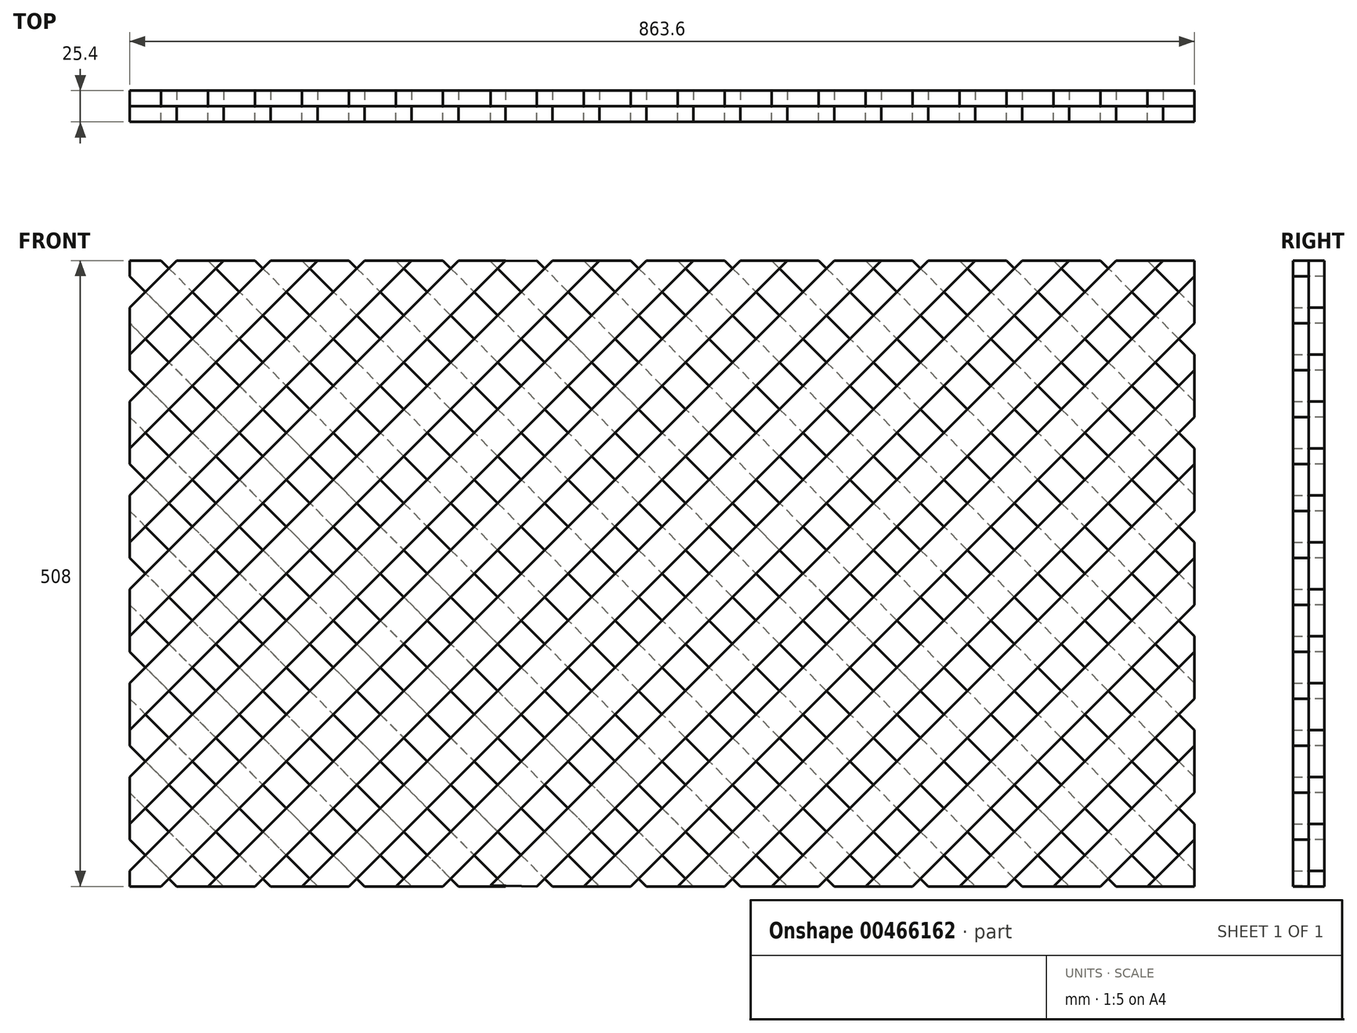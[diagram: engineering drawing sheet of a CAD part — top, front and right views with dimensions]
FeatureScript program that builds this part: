
annotation { "Feature Type Name" : "Feature", "Feature Type Description" : "" }
export const myFeature = defineFeature(function(context is Context, id is Id, definition is map)
    precondition{}
    {
        {
            var Q0;
            Q0=qCreatedBy(makeId("Front.planeOp"),FACE);
            var sketch = newSketch(context, id + "F0", { "sketchPlane" : qUnion([Q0])});
            skLineSegment(sketch, "E0.bottom", {"start": v(0, 0) * mm, "end": v(25.4, 0) * mm});
            skLineSegment(sketch, "E0.top", {"start": v(38.1, 508) * mm, "end": v(76.2, 508) * mm});
            skLineSegment(sketch, "E0.left", {"start": v(0, 0) * mm, "end": v(0, 12.7) * mm});
            skLineSegment(sketch, "E1", {"start": v(76.2, 508) * mm, "end": v(0, 431.8) * mm});
            skLineSegment(sketch, "E2", {"start": v(38.1, 393.7) * mm, "end": v(152.4, 508) * mm});
            skLineSegment(sketch, "E3", {"start": v(0, 355.6) * mm, "end": v(38.1, 393.7) * mm});
            skLineSegment(sketch, "E4", {"start": v(0, 279.4) * mm, "end": v(190.5, 469.9) * mm});
            skLineSegment(sketch, "E5", {"start": v(0, 203.2) * mm, "end": v(190.5, 393.7) * mm});
            skLineSegment(sketch, "E6", {"start": v(0, 127) * mm, "end": v(190.5, 317.5) * mm});
            skLineSegment(sketch, "E7", {"start": v(0, 50.8) * mm, "end": v(190.5, 241.3) * mm});
            skLineSegment(sketch, "E8", {"start": v(190.5, 165.1) * mm, "end": v(38.1, 12.7) * mm});
            skLineSegment(sketch, "E9", {"start": v(38.1, 12.7) * mm, "end": v(25.4, 0) * mm});
            skLineSegment(sketch, "E10", {"start": v(0, 469.9) * mm, "end": v(38.1, 508) * mm});
            skLineSegment(sketch, "E11", {"start": v(0, 393.7) * mm, "end": v(114.3, 508) * mm});
            skLineSegment(sketch, "E12", {"start": v(0, 317.5) * mm, "end": v(190.5, 508) * mm});
            skLineSegment(sketch, "E13", {"start": v(0, 241.3) * mm, "end": v(190.5, 431.8) * mm});
            skLineSegment(sketch, "E14", {"start": v(0, 165.1) * mm, "end": v(190.5, 355.6) * mm});
            skLineSegment(sketch, "E15", {"start": v(0, 88.9) * mm, "end": v(190.5, 279.4) * mm});
            skLineSegment(sketch, "E16", {"start": v(0, 12.7) * mm, "end": v(190.5, 203.2) * mm});
            skLineSegment(sketch, "E17", {"start": v(76.2, 12.7) * mm, "end": v(190.5, 127) * mm});
            skLineSegment(sketch, "E18", {"start": v(76.2, 12.7) * mm, "end": v(63.5, 0) * mm});
            skLineSegment(sketch, "E19", {"start": v(190.5, 88.9) * mm, "end": v(114.3, 12.7) * mm});
            skLineSegment(sketch, "E20", {"start": v(114.3, 12.7) * mm, "end": v(101.6, 0) * mm});
            skLineSegment(sketch, "E21", {"start": v(152.4, 12.7) * mm, "end": v(190.5, 50.8) * mm});
            skLineSegment(sketch, "E22", {"start": v(152.4, 12.7) * mm, "end": v(139.7, 0) * mm});
            skLineSegment(sketch, "E23", {"start": v(0, 431.8) * mm, "end": v(0, 469.9) * mm});
            skLineSegment(sketch, "E24", {"start": v(190.5, 12.7) * mm, "end": v(177.8, 0) * mm});
            skLineSegment(sketch, "E25.trimOffspring", {"start": v(139.7, 0) * mm, "end": v(177.8, 0) * mm});
            skLineSegment(sketch, "E26.trimOffspring", {"start": v(63.5, 0) * mm, "end": v(101.6, 0) * mm});
            skLineSegment(sketch, "E27.trimOffspring", {"start": v(0, 50.8) * mm, "end": v(0, 88.9) * mm});
            skLineSegment(sketch, "E28.trimOffspring", {"start": v(0, 127) * mm, "end": v(0, 165.1) * mm});
            skLineSegment(sketch, "E29.trimOffspring", {"start": v(0, 203.2) * mm, "end": v(0, 241.3) * mm});
            skLineSegment(sketch, "E30.trimOffspring", {"start": v(0, 355.6) * mm, "end": v(0, 393.7) * mm});
            skLineSegment(sketch, "E31.trimOffspring", {"start": v(114.3, 508) * mm, "end": v(152.4, 508) * mm});
            skLineSegment(sketch, "E32.1.0.1", {"start": v(190.5, 279.4) * mm, "end": v(381, 469.9) * mm});
            skLineSegment(sketch, "E32.1.0.3", {"start": v(190.5, 165.1) * mm, "end": v(381, 355.6) * mm});
            skLineSegment(sketch, "E32.1.0.4", {"start": v(190.5, 469.9) * mm, "end": v(228.6, 508) * mm});
            skLineSegment(sketch, "E32.1.0.5", {"start": v(190.5, 241.3) * mm, "end": v(381, 431.8) * mm});
            skLineSegment(sketch, "E32.1.0.7", {"start": v(190.5, 127) * mm, "end": v(381, 317.5) * mm});
            skLineSegment(sketch, "E32.1.0.8", {"start": v(381, 165.1) * mm, "end": v(228.6, 12.7) * mm});
            skLineSegment(sketch, "E32.1.0.11", {"start": v(190.5, 12.7) * mm, "end": v(381, 203.2) * mm});
            skLineSegment(sketch, "E32.1.0.14", {"start": v(266.7, 12.7) * mm, "end": v(381, 127) * mm});
            skLineSegment(sketch, "E32.1.0.15", {"start": v(190.5, 50.8) * mm, "end": v(381, 241.3) * mm});
            skLineSegment(sketch, "E32.1.0.18", {"start": v(190.5, 203.2) * mm, "end": v(381, 393.7) * mm});
            skLineSegment(sketch, "E32.1.0.19", {"start": v(342.9, 12.7) * mm, "end": v(381, 50.8) * mm});
            skLineSegment(sketch, "E32.1.0.24", {"start": v(190.5, 88.9) * mm, "end": v(381, 279.4) * mm});
            skLineSegment(sketch, "E32.1.0.25", {"start": v(381, 88.9) * mm, "end": v(304.8, 12.7) * mm});
            skLineSegment(sketch, "E32.1.0.28", {"start": v(190.5, 317.5) * mm, "end": v(381, 508) * mm});
            skLineSegment(sketch, "E32.1.0.30", {"start": v(190.5, 393.7) * mm, "end": v(304.8, 508) * mm});
            skLineSegment(sketch, "E32.1.0.32", {"start": v(190.5, 355.6) * mm, "end": v(228.6, 393.7) * mm});
            skLineSegment(sketch, "E32.1.0.33", {"start": v(228.6, 393.7) * mm, "end": v(342.9, 508) * mm});
            skLineSegment(sketch, "E32.1.0.34", {"start": v(266.7, 508) * mm, "end": v(190.5, 431.8) * mm});
            skLineSegment(sketch, "E32.1.0.36", {"start": v(266.7, 12.7) * mm, "end": v(254, 0) * mm});
            skLineSegment(sketch, "E32.1.0.37", {"start": v(228.6, 12.7) * mm, "end": v(215.9, 0) * mm});
            skLineSegment(sketch, "E32.1.0.39", {"start": v(342.9, 12.7) * mm, "end": v(330.2, 0) * mm});
            skLineSegment(sketch, "E32.1.0.40", {"start": v(381, 12.7) * mm, "end": v(368.3, 0) * mm});
            skLineSegment(sketch, "E32.1.0.41", {"start": v(304.8, 12.7) * mm, "end": v(292.1, 0) * mm});
            skLineSegment(sketch, "E32.2.0.1", {"start": v(381, 279.4) * mm, "end": v(571.5, 469.9) * mm});
            skLineSegment(sketch, "E32.2.0.3", {"start": v(381, 165.1) * mm, "end": v(571.5, 355.6) * mm});
            skLineSegment(sketch, "E32.2.0.4", {"start": v(381, 469.9) * mm, "end": v(419.1, 508) * mm});
            skLineSegment(sketch, "E32.2.0.5", {"start": v(381, 241.3) * mm, "end": v(571.5, 431.8) * mm});
            skLineSegment(sketch, "E32.2.0.7", {"start": v(381, 127) * mm, "end": v(571.5, 317.5) * mm});
            skLineSegment(sketch, "E32.2.0.8", {"start": v(571.5, 165.1) * mm, "end": v(419.1, 12.7) * mm});
            skLineSegment(sketch, "E32.2.0.11", {"start": v(381, 12.7) * mm, "end": v(571.5, 203.2) * mm});
            skLineSegment(sketch, "E32.2.0.12", {"start": v(495.3, 508) * mm, "end": v(533.4, 508) * mm});
            skLineSegment(sketch, "E32.2.0.14", {"start": v(457.2, 12.7) * mm, "end": v(571.5, 127) * mm});
            skLineSegment(sketch, "E32.2.0.15", {"start": v(381, 50.8) * mm, "end": v(571.5, 241.3) * mm});
            skLineSegment(sketch, "E32.2.0.18", {"start": v(381, 203.2) * mm, "end": v(571.5, 393.7) * mm});
            skLineSegment(sketch, "E32.2.0.19", {"start": v(533.4, 12.7) * mm, "end": v(571.5, 50.8) * mm});
            skLineSegment(sketch, "E32.2.0.21", {"start": v(444.5, 0) * mm, "end": v(482.6, 0) * mm});
            skLineSegment(sketch, "E32.2.0.24", {"start": v(381, 88.9) * mm, "end": v(571.5, 279.4) * mm});
            skLineSegment(sketch, "E32.2.0.25", {"start": v(571.5, 88.9) * mm, "end": v(495.3, 12.7) * mm});
            skLineSegment(sketch, "E32.2.0.28", {"start": v(381, 317.5) * mm, "end": v(571.5, 508) * mm});
            skLineSegment(sketch, "E32.2.0.29", {"start": v(520.7, 0) * mm, "end": v(558.8, 0) * mm});
            skLineSegment(sketch, "E32.2.0.30", {"start": v(381, 393.7) * mm, "end": v(495.3, 508) * mm});
            skLineSegment(sketch, "E32.2.0.31", {"start": v(419.1, 508) * mm, "end": v(457.2, 508) * mm});
            skLineSegment(sketch, "E32.2.0.32", {"start": v(381, 355.6) * mm, "end": v(419.1, 393.7) * mm});
            skLineSegment(sketch, "E32.2.0.33", {"start": v(419.1, 393.7) * mm, "end": v(533.4, 508) * mm});
            skLineSegment(sketch, "E32.2.0.34", {"start": v(457.2, 508) * mm, "end": v(381, 431.8) * mm});
            skLineSegment(sketch, "E32.2.0.35", {"start": v(381, 0) * mm, "end": v(406.4, 0) * mm});
            skLineSegment(sketch, "E32.2.0.36", {"start": v(457.2, 12.7) * mm, "end": v(444.5, 0) * mm});
            skLineSegment(sketch, "E32.2.0.37", {"start": v(419.1, 12.7) * mm, "end": v(406.4, 0) * mm});
            skLineSegment(sketch, "E32.2.0.39", {"start": v(533.4, 12.7) * mm, "end": v(520.7, 0) * mm});
            skLineSegment(sketch, "E32.2.0.40", {"start": v(571.5, 12.7) * mm, "end": v(558.8, 0) * mm});
            skLineSegment(sketch, "E32.2.0.41", {"start": v(495.3, 12.7) * mm, "end": v(482.6, 0) * mm});
            skLineSegment(sketch, "E32.3.0.1", {"start": v(571.5, 279.4) * mm, "end": v(762, 469.9) * mm});
            skLineSegment(sketch, "E32.3.0.3", {"start": v(571.5, 165.1) * mm, "end": v(762, 355.6) * mm});
            skLineSegment(sketch, "E32.3.0.4", {"start": v(571.5, 469.9) * mm, "end": v(609.6, 508) * mm});
            skLineSegment(sketch, "E32.3.0.5", {"start": v(571.5, 241.3) * mm, "end": v(762, 431.8) * mm});
            skLineSegment(sketch, "E32.3.0.7", {"start": v(571.5, 127) * mm, "end": v(762, 317.5) * mm});
            skLineSegment(sketch, "E32.3.0.8", {"start": v(762, 165.1) * mm, "end": v(609.6, 12.7) * mm});
            skLineSegment(sketch, "E32.3.0.11", {"start": v(571.5, 12.7) * mm, "end": v(762, 203.2) * mm});
            skLineSegment(sketch, "E32.3.0.14", {"start": v(647.7, 12.7) * mm, "end": v(762, 127) * mm});
            skLineSegment(sketch, "E32.3.0.15", {"start": v(571.5, 50.8) * mm, "end": v(762, 241.3) * mm});
            skLineSegment(sketch, "E32.3.0.18", {"start": v(571.5, 203.2) * mm, "end": v(762, 393.7) * mm});
            skLineSegment(sketch, "E32.3.0.19", {"start": v(723.9, 12.7) * mm, "end": v(762, 50.8) * mm});
            skLineSegment(sketch, "E32.3.0.24", {"start": v(571.5, 88.9) * mm, "end": v(762, 279.4) * mm});
            skLineSegment(sketch, "E32.3.0.25", {"start": v(762, 88.9) * mm, "end": v(685.8, 12.7) * mm});
            skLineSegment(sketch, "E32.3.0.28", {"start": v(571.5, 317.5) * mm, "end": v(762, 508) * mm});
            skLineSegment(sketch, "E32.3.0.30", {"start": v(571.5, 393.7) * mm, "end": v(685.8, 508) * mm});
            skLineSegment(sketch, "E32.3.0.32", {"start": v(571.5, 355.6) * mm, "end": v(609.6, 393.7) * mm});
            skLineSegment(sketch, "E32.3.0.33", {"start": v(609.6, 393.7) * mm, "end": v(723.9, 508) * mm});
            skLineSegment(sketch, "E32.3.0.34", {"start": v(647.7, 508) * mm, "end": v(571.5, 431.8) * mm});
            skLineSegment(sketch, "E32.3.0.36", {"start": v(647.7, 12.7) * mm, "end": v(635, 0) * mm});
            skLineSegment(sketch, "E32.3.0.37", {"start": v(609.6, 12.7) * mm, "end": v(596.9, 0) * mm});
            skLineSegment(sketch, "E32.3.0.39", {"start": v(723.9, 12.7) * mm, "end": v(711.2, 0) * mm});
            skLineSegment(sketch, "E32.3.0.40", {"start": v(762, 12.7) * mm, "end": v(749.3, 0) * mm});
            skLineSegment(sketch, "E32.3.0.41", {"start": v(685.8, 12.7) * mm, "end": v(673.1, 0) * mm});
            skLineSegment(sketch, "E32.4.0.1", {"start": v(762, 279.4) * mm, "end": v(863.6, 381) * mm});
            skLineSegment(sketch, "E32.4.0.3", {"start": v(762, 165.1) * mm, "end": v(863.6, 266.7) * mm});
            skLineSegment(sketch, "E32.4.0.4", {"start": v(762, 469.9) * mm, "end": v(800.1, 508) * mm});
            skLineSegment(sketch, "E32.4.0.5", {"start": v(762, 241.3) * mm, "end": v(863.6, 342.9) * mm});
            skLineSegment(sketch, "E32.4.0.7", {"start": v(762, 127) * mm, "end": v(863.6, 228.6) * mm});
            skLineSegment(sketch, "E32.4.0.8", {"start": v(863.6, 76.2) * mm, "end": v(800.1, 12.7) * mm});
            skLineSegment(sketch, "E32.4.0.11", {"start": v(762, 12.7) * mm, "end": v(863.6, 114.3) * mm});
            skLineSegment(sketch, "E32.4.0.14", {"start": v(838.2, 12.7) * mm, "end": v(863.6, 38.1) * mm});
            skLineSegment(sketch, "E32.4.0.15", {"start": v(762, 50.8) * mm, "end": v(863.6, 152.4) * mm});
            skLineSegment(sketch, "E32.4.0.18", {"start": v(762, 203.2) * mm, "end": v(863.6, 304.8) * mm});
            skLineSegment(sketch, "E32.4.0.21", {"start": v(825.5, 0) * mm, "end": v(863.6, 0) * mm});
            skLineSegment(sketch, "E32.4.0.24", {"start": v(762, 88.9) * mm, "end": v(863.6, 190.5) * mm});
            skLineSegment(sketch, "E32.4.0.28", {"start": v(762, 317.5) * mm, "end": v(863.6, 419.1) * mm});
            skLineSegment(sketch, "E32.4.0.30", {"start": v(762, 393.7) * mm, "end": v(863.6, 495.3) * mm});
            skLineSegment(sketch, "E32.4.0.31", {"start": v(800.1, 508) * mm, "end": v(838.2, 508) * mm});
            skLineSegment(sketch, "E32.4.0.32", {"start": v(762, 355.6) * mm, "end": v(800.1, 393.7) * mm});
            skLineSegment(sketch, "E32.4.0.33", {"start": v(800.1, 393.7) * mm, "end": v(863.6, 457.2) * mm});
            skLineSegment(sketch, "E32.4.0.34", {"start": v(838.2, 508) * mm, "end": v(762, 431.8) * mm});
            skLineSegment(sketch, "E32.4.0.35", {"start": v(762, 0) * mm, "end": v(787.4, 0) * mm});
            skLineSegment(sketch, "E32.4.0.36", {"start": v(838.2, 12.7) * mm, "end": v(825.5, 0) * mm});
            skLineSegment(sketch, "E32.4.0.37", {"start": v(800.1, 12.7) * mm, "end": v(787.4, 0) * mm});
            skLineSegment(sketch, "E32.direction1", {"start": v(0, 0) * mm, "end": v(177.8, 0) * mm, "construction": true});
            skLineSegment(sketch, "E33", {"start": v(190.5, 508) * mm, "end": v(228.6, 508) * mm});
            skLineSegment(sketch, "E34", {"start": v(266.7, 508) * mm, "end": v(304.8, 508) * mm});
            skLineSegment(sketch, "E35", {"start": v(342.9, 508) * mm, "end": v(381, 508) * mm});
            skLineSegment(sketch, "E36", {"start": v(215.9, 0) * mm, "end": v(254, 0) * mm});
            skLineSegment(sketch, "E37", {"start": v(292.21, 0.73) * mm, "end": v(330.2, 0) * mm});
            skLineSegment(sketch, "E38", {"start": v(368.3, 0) * mm, "end": v(381, 0) * mm});
            skLineSegment(sketch, "E39", {"start": v(0, 317.5) * mm, "end": v(0, 279.4) * mm});
            skLineSegment(sketch, "E40", {"start": v(762, 508) * mm, "end": v(723.9, 508) * mm});
            skLineSegment(sketch, "E41", {"start": v(685.8, 508) * mm, "end": v(647.7, 508) * mm});
            skLineSegment(sketch, "E42", {"start": v(609.6, 508) * mm, "end": v(571.5, 508) * mm});
            skLineSegment(sketch, "E43", {"start": v(762, 0) * mm, "end": v(749.3, 0) * mm});
            skLineSegment(sketch, "E44", {"start": v(596.9, 0) * mm, "end": v(635, 0) * mm});
            skLineSegment(sketch, "E45", {"start": v(673.1, 0) * mm, "end": v(711.2, 0) * mm});
            skLineSegment(sketch, "E46.0", {"start": v(863.6, 0) * mm, "end": v(863.6, 38.1) * mm});
            skLineSegment(sketch, "E47", {"start": v(863.6, 495.3) * mm, "end": v(863.6, 453.94) * mm});
            skLineSegment(sketch, "E48.trimOffspring", {"start": v(863.6, 381) * mm, "end": v(863.6, 419.1) * mm});
            skLineSegment(sketch, "E49.trimOffspring", {"start": v(863.6, 304.8) * mm, "end": v(863.6, 342.9) * mm});
            skLineSegment(sketch, "E50.trimOffspring", {"start": v(863.6, 228.6) * mm, "end": v(863.6, 266.7) * mm});
            skLineSegment(sketch, "E51.trimOffspring", {"start": v(863.6, 152.4) * mm, "end": v(863.6, 190.5) * mm});
            skLineSegment(sketch, "E52.trimOffspring", {"start": v(863.6, 76.2) * mm, "end": v(863.6, 114.3) * mm});
            skSolve(sketch);
        }
        {
            var Q0;
            Q0 = qSketchRegion(id + "F0", true);
            extrude(context, id + "F1", {"entities" : qUnion([Q0]), "depth" : 12.7 * mm});
        }
        {
            var Q0;
            Q0=qCreatedBy(makeId("Front.planeOp"),FACE);
            var sketch = newSketch(context, id + "F2", { "sketchPlane" : qUnion([Q0])});
            skLineSegment(sketch, "E53.MirrorCS", {"start": v(139.7, 508) * mm, "end": v(177.8, 508) * mm});
            skLineSegment(sketch, "E54.MirrorCS", {"start": v(63.5, 508) * mm, "end": v(101.6, 508) * mm});
            skLineSegment(sketch, "E55.MirrorCS", {"start": v(0, 508) * mm, "end": v(25.4, 508) * mm});
            skLineSegment(sketch, "E56.MirrorCS", {"start": v(0, 508) * mm, "end": v(0, 495.3) * mm});
            skLineSegment(sketch, "E57.MirrorCS", {"start": v(190.5, 495.3) * mm, "end": v(177.8, 508) * mm});
            skLineSegment(sketch, "E58.MirrorCS", {"start": v(685.8, 495.3) * mm, "end": v(673.1, 508) * mm});
            skLineSegment(sketch, "E59.MirrorCS", {"start": v(381, 508) * mm, "end": v(406.4, 508) * mm});
            skLineSegment(sketch, "E60.MirrorCS", {"start": v(457.2, 495.3) * mm, "end": v(444.5, 508) * mm});
            skLineSegment(sketch, "E61.MirrorCS", {"start": v(762, 508) * mm, "end": v(787.4, 508) * mm});
            skLineSegment(sketch, "E62.MirrorCS", {"start": v(762, 508) * mm, "end": v(749.3, 508) * mm});
            skLineSegment(sketch, "E63.MirrorCS", {"start": v(596.9, 508) * mm, "end": v(635, 508) * mm});
            skLineSegment(sketch, "E64.MirrorCS", {"start": v(838.2, 495.3) * mm, "end": v(825.5, 508) * mm});
            skLineSegment(sketch, "E65.MirrorCS", {"start": v(419.1, 495.3) * mm, "end": v(406.4, 508) * mm});
            skLineSegment(sketch, "E66.MirrorCS", {"start": v(533.4, 495.3) * mm, "end": v(520.7, 508) * mm});
            skLineSegment(sketch, "E67.MirrorCS", {"start": v(673.1, 508) * mm, "end": v(711.2, 508) * mm});
            skLineSegment(sketch, "E68.MirrorCS", {"start": v(800.1, 495.3) * mm, "end": v(787.4, 508) * mm});
            skLineSegment(sketch, "E69.MirrorCS", {"start": v(571.5, 495.3) * mm, "end": v(558.8, 508) * mm});
            skLineSegment(sketch, "E70.MirrorCS", {"start": v(76.2, 495.3) * mm, "end": v(63.5, 508) * mm});
            skLineSegment(sketch, "E71.MirrorCS", {"start": v(495.3, 495.3) * mm, "end": v(482.6, 508) * mm});
            skLineSegment(sketch, "E72.MirrorCS", {"start": v(266.7, 495.3) * mm, "end": v(254, 508) * mm});
            skLineSegment(sketch, "E73.MirrorCS", {"start": v(444.5, 508) * mm, "end": v(482.6, 508) * mm});
            skLineSegment(sketch, "E74.MirrorCS", {"start": v(228.6, 495.3) * mm, "end": v(215.9, 508) * mm});
            skLineSegment(sketch, "E75.MirrorCS", {"start": v(114.3, 495.3) * mm, "end": v(101.6, 508) * mm});
            skLineSegment(sketch, "E76.MirrorCS", {"start": v(342.9, 495.3) * mm, "end": v(330.2, 508) * mm});
            skLineSegment(sketch, "E77.MirrorCS", {"start": v(381, 495.3) * mm, "end": v(368.3, 508) * mm});
            skLineSegment(sketch, "E78.MirrorCS", {"start": v(825.5, 508) * mm, "end": v(863.6, 508) * mm});
            skLineSegment(sketch, "E79.MirrorCS", {"start": v(647.7, 495.3) * mm, "end": v(635, 508) * mm});
            skLineSegment(sketch, "E80.MirrorCS", {"start": v(304.8, 495.3) * mm, "end": v(292.1, 508) * mm});
            skLineSegment(sketch, "E81.MirrorCS", {"start": v(152.4, 495.3) * mm, "end": v(139.7, 508) * mm});
            skLineSegment(sketch, "E82.MirrorCS", {"start": v(215.9, 508) * mm, "end": v(254, 508) * mm});
            skLineSegment(sketch, "E83.MirrorCS", {"start": v(609.6, 495.3) * mm, "end": v(596.9, 508) * mm});
            skLineSegment(sketch, "E84.MirrorCS", {"start": v(38.1, 495.3) * mm, "end": v(25.4, 508) * mm});
            skLineSegment(sketch, "E85.MirrorCS", {"start": v(520.7, 508) * mm, "end": v(558.8, 508) * mm});
            skLineSegment(sketch, "E86.MirrorCS", {"start": v(292.21, 507.27) * mm, "end": v(330.2, 508) * mm});
            skLineSegment(sketch, "E87.MirrorCS", {"start": v(723.9, 495.3) * mm, "end": v(711.2, 508) * mm});
            skLineSegment(sketch, "E88.MirrorCS", {"start": v(368.3, 508) * mm, "end": v(381, 508) * mm});
            skLineSegment(sketch, "E89.MirrorCS", {"start": v(762, 495.3) * mm, "end": v(749.3, 508) * mm});
            skLineSegment(sketch, "E90.MirrorCS", {"start": v(419.1, 0) * mm, "end": v(457.2, 0) * mm});
            skLineSegment(sketch, "E91.MirrorCS", {"start": v(381, 38.1) * mm, "end": v(419.1, 0) * mm});
            skLineSegment(sketch, "E92.MirrorCS", {"start": v(190.5, 304.8) * mm, "end": v(381, 114.3) * mm});
            skLineSegment(sketch, "E93.MirrorCS", {"start": v(0, 190.5) * mm, "end": v(0, 228.6) * mm});
            skLineSegment(sketch, "E94.MirrorCS", {"start": v(762, 114.3) * mm, "end": v(863.6, 12.7) * mm});
            skLineSegment(sketch, "E95.MirrorCS", {"start": v(571.5, 495.3) * mm, "end": v(762, 304.8) * mm});
            skLineSegment(sketch, "E96.MirrorCS", {"start": v(0, 457.2) * mm, "end": v(0, 419.1) * mm});
            skLineSegment(sketch, "E97.MirrorCS", {"start": v(571.5, 457.2) * mm, "end": v(762, 266.7) * mm});
            skLineSegment(sketch, "E98.MirrorCS", {"start": v(419.1, 114.3) * mm, "end": v(533.4, 0) * mm});
            skLineSegment(sketch, "E99.MirrorCS", {"start": v(381, 381) * mm, "end": v(571.5, 190.5) * mm});
            skLineSegment(sketch, "E100.MirrorCS", {"start": v(190.5, 419.1) * mm, "end": v(381, 228.6) * mm});
            skLineSegment(sketch, "E101.MirrorCS", {"start": v(762, 0) * mm, "end": v(723.9, 0) * mm});
            skLineSegment(sketch, "E102.MirrorCS", {"start": v(762, 152.4) * mm, "end": v(800.1, 114.3) * mm});
            skLineSegment(sketch, "E103.MirrorCS", {"start": v(762, 342.9) * mm, "end": v(863.6, 241.3) * mm});
            skLineSegment(sketch, "E104.MirrorCS", {"start": v(381, 152.4) * mm, "end": v(419.1, 114.3) * mm});
            skLineSegment(sketch, "E105.MirrorCS", {"start": v(381, 266.7) * mm, "end": v(571.5, 76.2) * mm});
            skLineSegment(sketch, "E106.MirrorCS", {"start": v(342.9, 495.3) * mm, "end": v(381, 457.2) * mm});
            skLineSegment(sketch, "E107.MirrorCS", {"start": v(800.1, 0) * mm, "end": v(838.2, 0) * mm});
            skLineSegment(sketch, "E108.MirrorCS", {"start": v(647.7, 495.3) * mm, "end": v(762, 381) * mm});
            skLineSegment(sketch, "E109.MirrorCS", {"start": v(762, 228.6) * mm, "end": v(863.6, 127) * mm});
            skLineSegment(sketch, "E110.MirrorCS", {"start": v(0, 381) * mm, "end": v(0, 342.9) * mm});
            skLineSegment(sketch, "E111.MirrorCS", {"start": v(457.2, 0) * mm, "end": v(381, 76.2) * mm});
            skLineSegment(sketch, "E112.MirrorCS", {"start": v(571.5, 304.8) * mm, "end": v(762, 114.3) * mm});
            skLineSegment(sketch, "E113.MirrorCS", {"start": v(381, 419.1) * mm, "end": v(304.8, 495.3) * mm});
            skLineSegment(sketch, "E114.MirrorCS", {"start": v(571.5, 342.9) * mm, "end": v(419.1, 495.3) * mm});
            skLineSegment(sketch, "E115.MirrorCS", {"start": v(685.8, 0) * mm, "end": v(647.7, 0) * mm});
            skLineSegment(sketch, "E116.MirrorCS", {"start": v(800.1, 114.3) * mm, "end": v(863.6, 50.8) * mm});
            skLineSegment(sketch, "E117.MirrorCS", {"start": v(762, 38.1) * mm, "end": v(800.1, 0) * mm});
            skLineSegment(sketch, "E118.MirrorCS", {"start": v(0, 304.8) * mm, "end": v(0, 266.7) * mm});
            skLineSegment(sketch, "E119.MirrorCS", {"start": v(723.9, 495.3) * mm, "end": v(762, 457.2) * mm});
            skLineSegment(sketch, "E120.MirrorCS", {"start": v(381, 495.3) * mm, "end": v(571.5, 304.8) * mm});
            skLineSegment(sketch, "E121.MirrorCS", {"start": v(190.5, 190.5) * mm, "end": v(381, 0) * mm});
            skLineSegment(sketch, "E122.MirrorCS", {"start": v(838.2, 0) * mm, "end": v(762, 76.2) * mm});
            skLineSegment(sketch, "E123.MirrorCS", {"start": v(609.6, 0) * mm, "end": v(571.5, 0) * mm});
            skLineSegment(sketch, "E124.MirrorCS", {"start": v(762, 266.7) * mm, "end": v(863.6, 165.1) * mm});
            skLineSegment(sketch, "E125.MirrorCS", {"start": v(571.5, 419.1) * mm, "end": v(762, 228.6) * mm});
            skLineSegment(sketch, "E126.MirrorCS", {"start": v(495.3, 0) * mm, "end": v(533.4, 0) * mm});
            skLineSegment(sketch, "E127.MirrorCS", {"start": v(190.5, 114.3) * mm, "end": v(304.8, 0) * mm});
            skLineSegment(sketch, "E128.MirrorCS", {"start": v(762, 381) * mm, "end": v(863.6, 279.4) * mm});
            skLineSegment(sketch, "E129.MirrorCS", {"start": v(0, 152.4) * mm, "end": v(0, 114.3) * mm});
            skLineSegment(sketch, "E130.MirrorCS", {"start": v(0, 342.9) * mm, "end": v(190.5, 152.4) * mm});
            skLineSegment(sketch, "E131.MirrorCS", {"start": v(863.6, 431.8) * mm, "end": v(800.1, 495.3) * mm});
            skLineSegment(sketch, "E132.MirrorCS", {"start": v(114.3, 0) * mm, "end": v(152.4, 0) * mm});
            skLineSegment(sketch, "E133.MirrorCS", {"start": v(0, 419.1) * mm, "end": v(190.5, 228.6) * mm});
            skLineSegment(sketch, "E134.MirrorCS", {"start": v(762, 419.1) * mm, "end": v(685.8, 495.3) * mm});
            skLineSegment(sketch, "E135.MirrorCS", {"start": v(190.5, 152.4) * mm, "end": v(228.6, 114.3) * mm});
            skLineSegment(sketch, "E136.MirrorCS", {"start": v(457.2, 495.3) * mm, "end": v(571.5, 381) * mm});
            skLineSegment(sketch, "E137.MirrorCS", {"start": v(190.5, 228.6) * mm, "end": v(381, 38.1) * mm});
            skLineSegment(sketch, "E138.MirrorCS", {"start": v(0, 495.3) * mm, "end": v(190.5, 304.8) * mm});
            skLineSegment(sketch, "E139.MirrorCS", {"start": v(571.5, 190.5) * mm, "end": v(762, 0) * mm});
            skLineSegment(sketch, "E140.MirrorCS", {"start": v(381, 457.2) * mm, "end": v(571.5, 266.7) * mm});
            skLineSegment(sketch, "E141.MirrorCS", {"start": v(228.6, 114.3) * mm, "end": v(342.9, 0) * mm});
            skLineSegment(sketch, "E142.MirrorCS", {"start": v(762, 495.3) * mm, "end": v(863.6, 393.7) * mm});
            skLineSegment(sketch, "E143.MirrorCS", {"start": v(190.5, 342.9) * mm, "end": v(381, 152.4) * mm});
            skLineSegment(sketch, "E144.MirrorCS", {"start": v(76.2, 495.3) * mm, "end": v(190.5, 381) * mm});
            skLineSegment(sketch, "E145.MirrorCS", {"start": v(571.5, 114.3) * mm, "end": v(685.8, 0) * mm});
            skLineSegment(sketch, "E146.MirrorCS", {"start": v(381, 304.8) * mm, "end": v(571.5, 114.3) * mm});
            skLineSegment(sketch, "E147.MirrorCS", {"start": v(266.7, 0) * mm, "end": v(190.5, 76.2) * mm});
            skLineSegment(sketch, "E148.MirrorCS", {"start": v(190.5, 38.1) * mm, "end": v(228.6, 0) * mm});
            skLineSegment(sketch, "E149.MirrorCS", {"start": v(571.5, 152.4) * mm, "end": v(609.6, 114.3) * mm});
            skLineSegment(sketch, "E150.MirrorCS", {"start": v(533.4, 495.3) * mm, "end": v(571.5, 457.2) * mm});
            skLineSegment(sketch, "E151.MirrorCS", {"start": v(838.2, 495.3) * mm, "end": v(863.6, 469.9) * mm});
            skLineSegment(sketch, "E152.MirrorCS", {"start": v(190.5, 266.7) * mm, "end": v(381, 76.2) * mm});
            skLineSegment(sketch, "E153.MirrorCS", {"start": v(190.5, 419.1) * mm, "end": v(114.3, 495.3) * mm});
            skLineSegment(sketch, "E154.MirrorCS", {"start": v(609.6, 114.3) * mm, "end": v(723.9, 0) * mm});
            skLineSegment(sketch, "E155.MirrorCS", {"start": v(571.5, 228.6) * mm, "end": v(762, 38.1) * mm});
            skLineSegment(sketch, "E156.MirrorCS", {"start": v(190.5, 0) * mm, "end": v(228.6, 0) * mm});
            skLineSegment(sketch, "E157.MirrorCS", {"start": v(762, 457.2) * mm, "end": v(863.6, 355.6) * mm});
            skLineSegment(sketch, "E158.MirrorCS", {"start": v(190.5, 381) * mm, "end": v(381, 190.5) * mm});
            skLineSegment(sketch, "E159.MirrorCS", {"start": v(647.7, 0) * mm, "end": v(571.5, 76.2) * mm});
            skLineSegment(sketch, "E160.MirrorCS", {"start": v(571.5, 342.9) * mm, "end": v(762, 152.4) * mm});
            skLineSegment(sketch, "E161.MirrorCS", {"start": v(381, 419.1) * mm, "end": v(571.5, 228.6) * mm});
            skLineSegment(sketch, "E162.MirrorCS", {"start": v(266.7, 0) * mm, "end": v(304.8, 0) * mm});
            skLineSegment(sketch, "E163.MirrorCS", {"start": v(762, 304.8) * mm, "end": v(863.6, 203.2) * mm});
            skLineSegment(sketch, "E164.MirrorCS", {"start": v(571.5, 419.1) * mm, "end": v(495.3, 495.3) * mm});
            skLineSegment(sketch, "E165.MirrorCS", {"start": v(381, 342.9) * mm, "end": v(228.6, 495.3) * mm});
            skLineSegment(sketch, "E166.MirrorCS", {"start": v(152.4, 495.3) * mm, "end": v(190.5, 457.2) * mm});
            skLineSegment(sketch, "E167.MirrorCS", {"start": v(342.9, 0) * mm, "end": v(381, 0) * mm});
            skLineSegment(sketch, "E168.MirrorCS", {"start": v(571.5, 38.1) * mm, "end": v(609.6, 0) * mm});
            skLineSegment(sketch, "E169.MirrorCS", {"start": v(381, 190.5) * mm, "end": v(571.5, 0) * mm});
            skLineSegment(sketch, "E170.MirrorCS", {"start": v(190.5, 495.3) * mm, "end": v(381, 304.8) * mm});
            skLineSegment(sketch, "E171.MirrorCS", {"start": v(762, 419.1) * mm, "end": v(863.6, 317.5) * mm});
            skLineSegment(sketch, "E172.MirrorCS", {"start": v(571.5, 266.7) * mm, "end": v(762, 76.2) * mm});
            skLineSegment(sketch, "E173.MirrorCS", {"start": v(0, 114.3) * mm, "end": v(114.3, 0) * mm});
            skLineSegment(sketch, "E174.MirrorCS", {"start": v(0, 190.5) * mm, "end": v(190.5, 0) * mm});
            skLineSegment(sketch, "E175.MirrorCS", {"start": v(0, 266.7) * mm, "end": v(190.5, 76.2) * mm});
            skLineSegment(sketch, "E176.MirrorCS", {"start": v(38.1, 0) * mm, "end": v(76.2, 0) * mm});
            skLineSegment(sketch, "E177.MirrorCS", {"start": v(76.2, 0) * mm, "end": v(0, 76.2) * mm});
            skLineSegment(sketch, "E178.MirrorCS", {"start": v(38.1, 114.3) * mm, "end": v(152.4, 0) * mm});
            skLineSegment(sketch, "E179.MirrorCS", {"start": v(0, 152.4) * mm, "end": v(38.1, 114.3) * mm});
            skLineSegment(sketch, "E180.MirrorCS", {"start": v(0, 228.6) * mm, "end": v(190.5, 38.1) * mm});
            skLineSegment(sketch, "E181.MirrorCS", {"start": v(0, 304.8) * mm, "end": v(190.5, 114.3) * mm});
            skLineSegment(sketch, "E182.MirrorCS", {"start": v(0, 381) * mm, "end": v(190.5, 190.5) * mm});
            skLineSegment(sketch, "E183.MirrorCS", {"start": v(0, 457.2) * mm, "end": v(190.5, 266.7) * mm});
            skLineSegment(sketch, "E184.MirrorCS", {"start": v(190.5, 342.9) * mm, "end": v(38.1, 495.3) * mm});
            skLineSegment(sketch, "E185.MirrorCS", {"start": v(381, 228.6) * mm, "end": v(571.5, 38.1) * mm});
            skLineSegment(sketch, "E186.MirrorCS", {"start": v(266.7, 495.3) * mm, "end": v(381, 381) * mm});
            skLineSegment(sketch, "E187.MirrorCS", {"start": v(0, 76.2) * mm, "end": v(0, 38.1) * mm});
            skLineSegment(sketch, "E188.MirrorCS", {"start": v(0, 38.1) * mm, "end": v(38.1, 0) * mm});
            skLineSegment(sketch, "E189.MirrorCS", {"start": v(571.5, 381) * mm, "end": v(762, 190.5) * mm});
            skLineSegment(sketch, "E190.MirrorCS", {"start": v(381, 114.3) * mm, "end": v(495.3, 0) * mm});
            skLineSegment(sketch, "E191.MirrorCS", {"start": v(381, 342.9) * mm, "end": v(571.5, 152.4) * mm});
            skLineSegment(sketch, "E192.MirrorCS", {"start": v(190.5, 457.2) * mm, "end": v(381, 266.7) * mm});
            skLineSegment(sketch, "E193.MirrorCS", {"start": v(762, 190.5) * mm, "end": v(863.6, 88.9) * mm});
            skLineSegment(sketch, "E194.MirrorCS", {"start": v(762, 342.9) * mm, "end": v(609.6, 495.3) * mm});
            skLineSegment(sketch, "E195", {"start": v(863.6, 508) * mm, "end": v(863.6, 469.9) * mm});
            skLineSegment(sketch, "E196.trimOffspring", {"start": v(863.6, 431.8) * mm, "end": v(863.6, 393.7) * mm});
            skLineSegment(sketch, "E197.trimOffspring", {"start": v(863.6, 355.6) * mm, "end": v(863.6, 317.5) * mm});
            skLineSegment(sketch, "E198.trimOffspring", {"start": v(863.6, 279.4) * mm, "end": v(863.6, 241.3) * mm});
            skLineSegment(sketch, "E199.trimOffspring", {"start": v(863.6, 203.2) * mm, "end": v(863.6, 165.1) * mm});
            skLineSegment(sketch, "E200.trimOffspring", {"start": v(863.6, 127) * mm, "end": v(863.6, 88.9) * mm});
            skLineSegment(sketch, "E201.trimOffspring", {"start": v(863.6, 50.8) * mm, "end": v(863.6, 12.7) * mm});
            skSolve(sketch);
        }
        {
            var Q0;
            Q0 = qSketchRegion(id + "F2", true);
            extrude(context, id + "F3", {"entities" : qUnion([Q0]), "oppositeDirection" : true, "depth" : 12.7 * mm});
        }
    });
